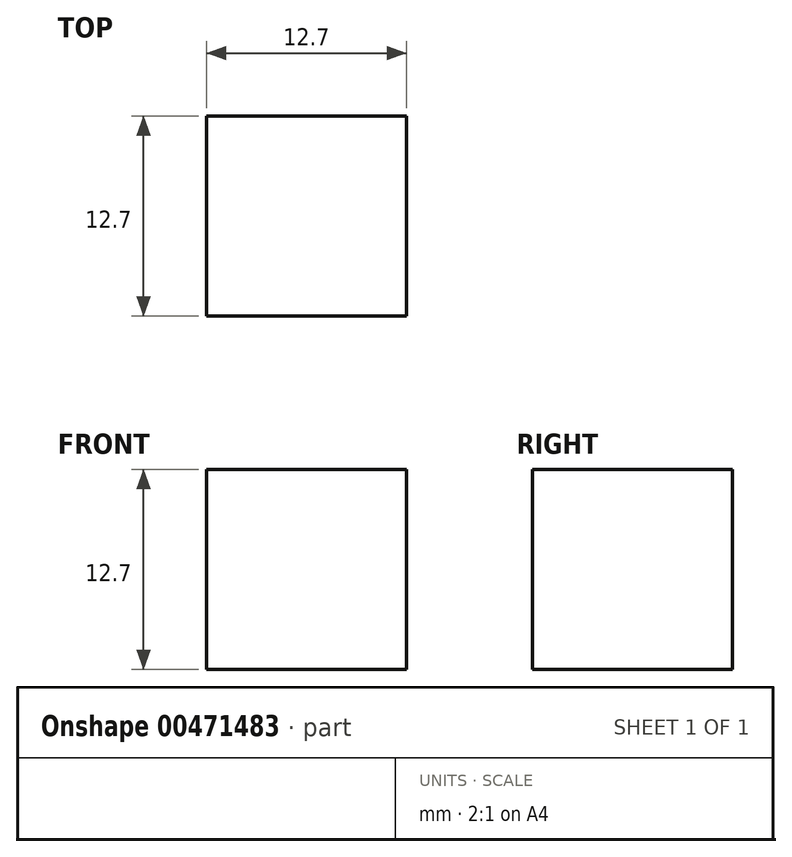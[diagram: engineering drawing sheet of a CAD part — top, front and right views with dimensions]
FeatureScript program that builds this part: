
annotation { "Feature Type Name" : "Feature", "Feature Type Description" : "" }
export const myFeature = defineFeature(function(context is Context, id is Id, definition is map)
    precondition{}
    {
        {
            var Q0;
            Q0=qCreatedBy(makeId("Top.planeOp"),FACE);
            var sketch = newSketch(context, id + "F0", { "sketchPlane" : qUnion([Q0])});
            skLineSegment(sketch, "E0.bottom", {"start": v(6.96, -10.54) * mm, "end": v(19.66, -10.54) * mm});
            skLineSegment(sketch, "E0.top", {"start": v(6.96, -23.24) * mm, "end": v(19.66, -23.24) * mm});
            skLineSegment(sketch, "E0.left", {"start": v(6.96, -10.54) * mm, "end": v(6.96, -23.24) * mm});
            skLineSegment(sketch, "E0.right", {"start": v(19.66, -10.54) * mm, "end": v(19.66, -23.24) * mm});
            skSolve(sketch);
        }
        {
            var Q0;
            Q0=makeQuery(id+"F0.imprint","IMPRINT",FACE,{"disambiguationData":[TD([[makeQuery(id+"F0.imprint","IMPRINT",EDGE,{"derivedFrom":sQuery(id+"F0.wireOp",EDGE,"E0.bottom")}),-1.0]])]});
            extrude(context, id + "F1", {"entities" : qUnion([Q0]), "depth" : 12.7 * mm});
        }
    });
